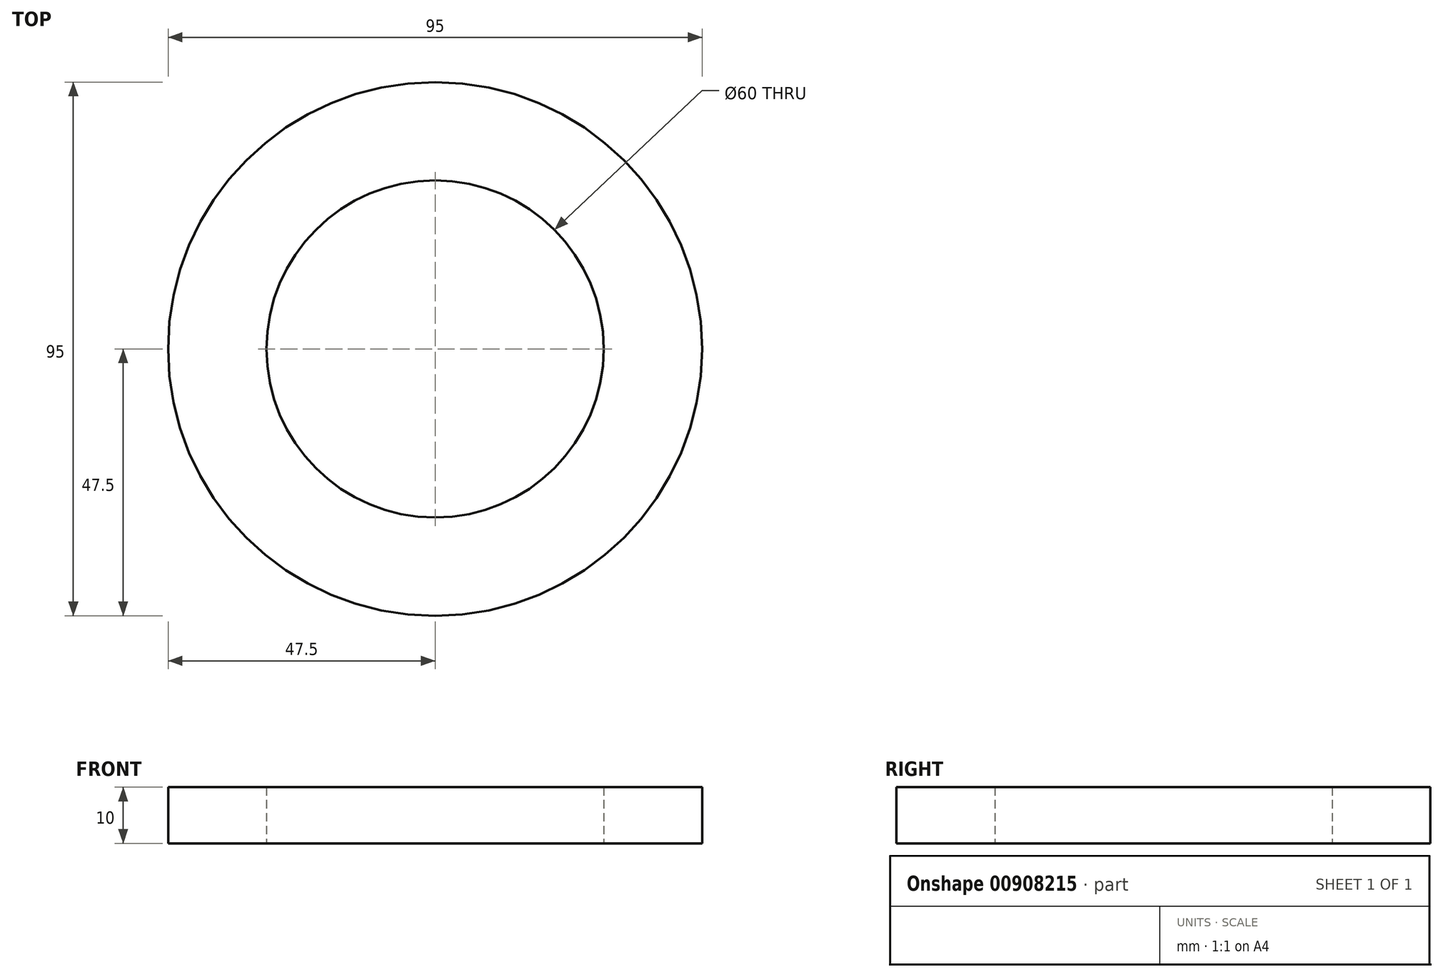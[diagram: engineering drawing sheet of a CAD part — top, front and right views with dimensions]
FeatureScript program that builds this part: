
annotation { "Feature Type Name" : "Feature", "Feature Type Description" : "" }
export const myFeature = defineFeature(function(context is Context, id is Id, definition is map)
    precondition{}
    {
        {
            var Q0;
            Q0=qCreatedBy(makeId("Top.planeOp"),FACE);
            var sketch = newSketch(context, id + "F0", { "sketchPlane" : qUnion([Q0])});
            skCircle(sketch, "E0", {"center": v(0, 0) * mm, "radius": 30 * mm});
            skCircle(sketch, "E1", {"center": v(0, 0) * mm, "radius": 47.5 * mm});
            skSolve(sketch);
        }
        {
            var Q0;
            Q0 = qSketchRegion(id + "F0", true);
            extrude(context, id + "F1", {"entities" : qUnion([Q0]), "depth" : 10 * mm, "offsetDistance" : 25 * mm});
        }
    });
